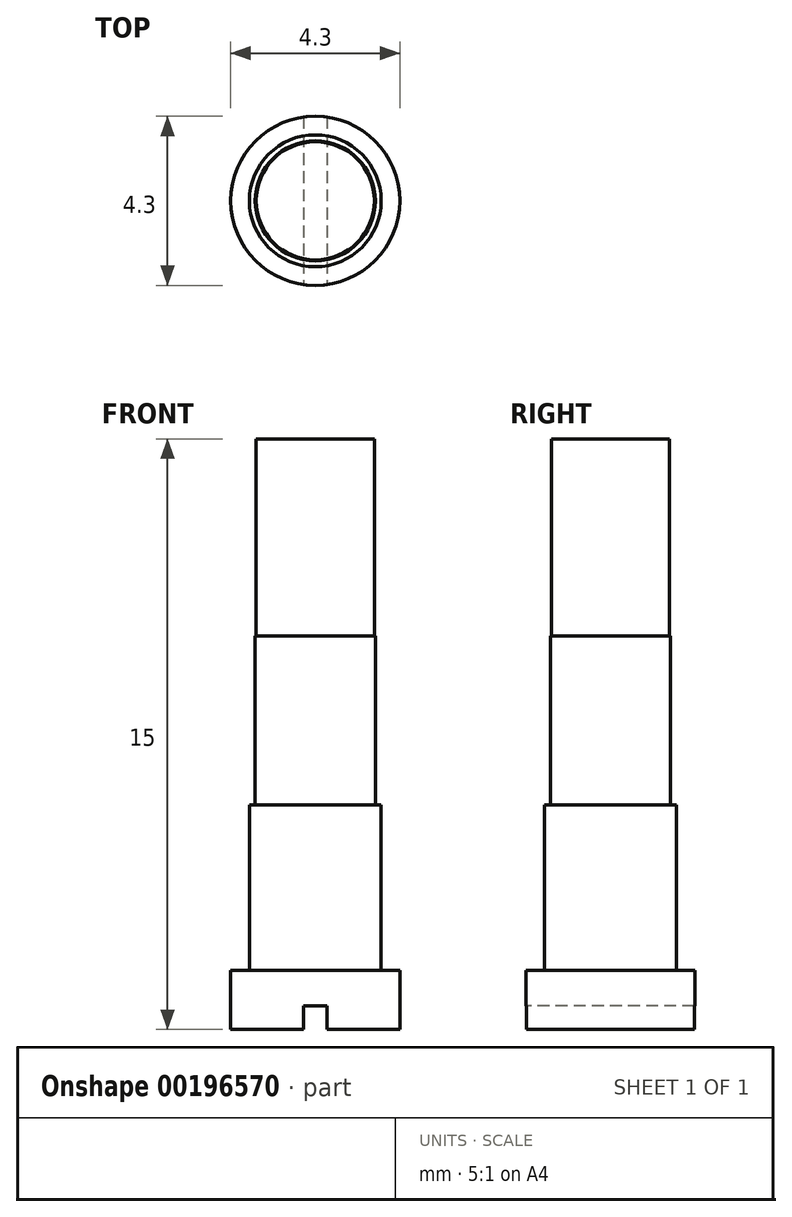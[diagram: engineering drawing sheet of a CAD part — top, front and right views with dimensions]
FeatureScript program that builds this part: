
annotation { "Feature Type Name" : "Feature", "Feature Type Description" : "" }
export const myFeature = defineFeature(function(context is Context, id is Id, definition is map)
    precondition{}
    {
        {
            var Q0;
            Q0=qCreatedBy(makeId("Front.planeOp"),FACE);
            var sketch = newSketch(context, id + "F0", { "sketchPlane" : qUnion([Q0])});
            skLineSegment(sketch, "E0", {"start": v(0, 0) * mm, "end": v(2.15, 0) * mm});
            skLineSegment(sketch, "E1", {"start": v(2.15, 0) * mm, "end": v(2.15, 1.5) * mm});
            skLineSegment(sketch, "E2", {"start": v(2.15, 1.5) * mm, "end": v(1.68, 1.5) * mm});
            skLineSegment(sketch, "E3", {"start": v(1.68, 1.5) * mm, "end": v(1.67, 5.7) * mm});
            skLineSegment(sketch, "E4", {"start": v(1.68, 5.7) * mm, "end": v(1.53, 5.7) * mm});
            skLineSegment(sketch, "E5", {"start": v(1.53, 5.7) * mm, "end": v(1.52, 10) * mm});
            skLineSegment(sketch, "E6", {"start": v(1.52, 10) * mm, "end": v(1.5, 10) * mm});
            skLineSegment(sketch, "E7", {"start": v(1.5, 10) * mm, "end": v(1.5, 15) * mm});
            skLineSegment(sketch, "E8", {"start": v(0, 17.76) * mm, "end": v(0, 0) * mm, "construction": true});
            skLineSegment(sketch, "E9", {"start": v(1.5, 15) * mm, "end": v(0, 15) * mm});
            skLineSegment(sketch, "E10", {"start": v(0, 0) * mm, "end": v(0, 15) * mm});
            skSolve(sketch);
        }
        {
            var Q0;
            Q0 = qSketchRegion(id + "F0", true);
            var Q1;
            Q1=sQuery(id+"F0.wireOp",EDGE,"E8");
            revolve(context, id + "F1", {"entities" : qUnion([Q0]), "axis" : qUnion([Q1]), "revolveType" : RevolveType.FULL});
        }
        {
            var Q0;
            Q0=qCreatedBy(makeId("Front.planeOp"),FACE);
            var sketch = newSketch(context, id + "F2", { "sketchPlane" : qUnion([Q0])});
            skLineSegment(sketch, "E11", {"start": v(-0.3, 0) * mm, "end": v(-0.3, 0.6) * mm});
            skLineSegment(sketch, "E12.MirrorCS", {"start": v(0.3, 0) * mm, "end": v(0.3, 0.6) * mm});
            skLineSegment(sketch, "E13", {"start": v(-0.3, 0.6) * mm, "end": v(0.3, 0.6) * mm});
            skLineSegment(sketch, "E14", {"start": v(0.3, 0) * mm, "end": v(-0.3, 0) * mm});
            skSolve(sketch);
        }
        {
            var Q0;
            Q0 = qSketchRegion(id + "F2", true);
            extrude(context, id + "F3", {"entities" : qUnion([Q0]), "operationType" : NewBodyOperationType.REMOVE, "endBound" : BoundingType.THROUGH_ALL, "oppositeDirection" : true, "depth" : 25 * mm, "hasSecondDirection" : true, "secondDirectionBound" : SecondDirectionBoundingType.THROUGH_ALL, "secondDirectionOppositeDirection" : false, "secondDirectionDepth" : 25 * mm});
        }
    });
